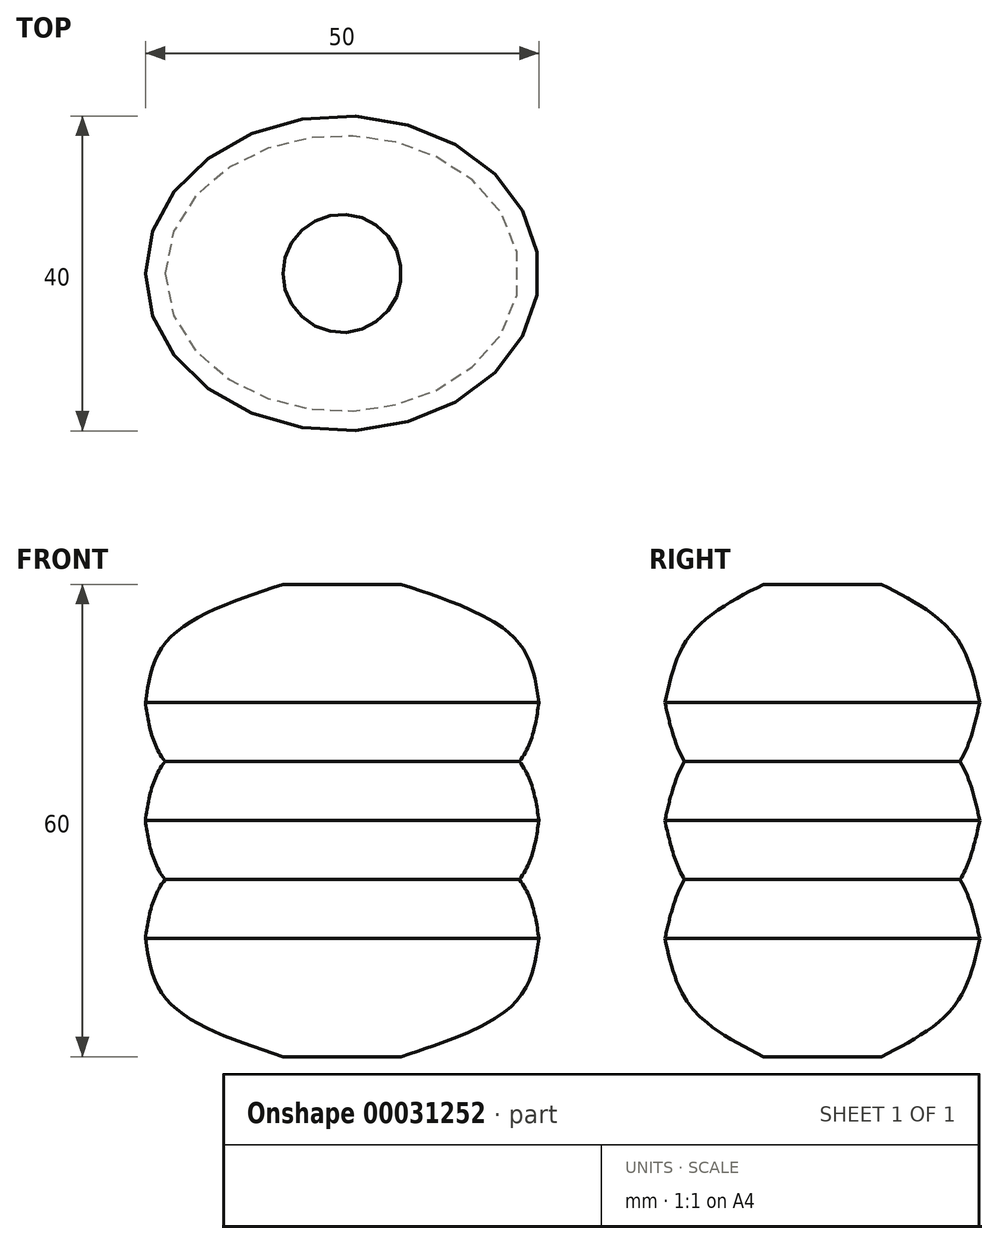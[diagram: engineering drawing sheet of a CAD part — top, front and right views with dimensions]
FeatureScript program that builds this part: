
annotation { "Feature Type Name" : "Feature", "Feature Type Description" : "" }
export const myFeature = defineFeature(function(context is Context, id is Id, definition is map)
    precondition{}
    {
        {
            var Q0;
            Q0=qCreatedBy(makeId("Top.planeOp"),FACE);
            var sketch = newSketch(context, id + "F0", { "sketchPlane" : qUnion([Q0])});
            skEllipse(sketch, "E0", {"center": v(0, 0) * mm, "majorRadius": 20 * mm, "minorRadius": 25 * mm, "majorAxis": v(0, 1)});
            skPoint(sketch, "E1", {"position": v(0, 20) * mm});
            skPoint(sketch, "E2", {"position": v(-25, 0) * mm});
            skSolve(sketch);
        }
        {
            var Q0;
            Q0=qCreatedBy(makeId("Top.planeOp"),FACE);
            cPlane(context, id + "F1", {"entities" : qUnion([Q0]), "cplaneType" : CPlaneType.OFFSET, "offset" : 15 * mm, "width" : 150 * mm, "height" : 150 * mm});
        }
        {
            var Q0;
            Q0=qCreatedBy(id+"F1.planeOp",FACE);
            var sketch = newSketch(context, id + "F2", { "sketchPlane" : qUnion([Q0])});
            skCircle(sketch, "E3", {"center": v(0, 0) * mm, "radius": 7.5 * mm});
            skSolve(sketch);
        }
        {
            var Q0;
            Q0=qCreatedBy(makeId("Top.planeOp"),FACE);
            cPlane(context, id + "F3", {"entities" : qUnion([Q0]), "cplaneType" : CPlaneType.OFFSET, "offset" : 7.5 * mm, "width" : 150 * mm, "height" : 150 * mm});
        }
        {
            var Q0;
            Q0=qCreatedBy(id+"F3.planeOp",FACE);
            var sketch = newSketch(context, id + "F4", { "sketchPlane" : qUnion([Q0])});
            skEllipse(sketch, "E4", {"center": v(0, 0) * mm, "majorRadius": 17.5 * mm, "minorRadius": 22.5 * mm, "majorAxis": v(0, -1)});
            skPoint(sketch, "E5", {"position": v(0, -17.5) * mm});
            skPoint(sketch, "E6", {"position": v(-22.5, 0) * mm});
            skSolve(sketch);
        }
        {
            var Q0;
            Q0=makeQuery(id+"F0.imprint","IMPRINT",FACE,{"disambiguationData":[TD([[makeQuery(id+"F0.imprint","IMPRINT",EDGE,{"derivedFrom":sQuery(id+"F0.wireOp",EDGE,"E0")}),1.0]])]});
            var Q1;
            Q1=makeQuery(id+"F4.imprint","IMPRINT",FACE,{"disambiguationData":[TD([[makeQuery(id+"F4.imprint","IMPRINT",EDGE,{"derivedFrom":sQuery(id+"F4.wireOp",EDGE,"E4")}),1.0]])]});
            var Q2;
            Q2=makeQuery(id+"F2.imprint","IMPRINT",FACE,{"disambiguationData":[TD([[makeQuery(id+"F2.imprint","IMPRINT",EDGE,{"derivedFrom":sQuery(id+"F2.wireOp",EDGE,"E3")}),1.0]])]});
            loft(context, id + "F5", {"sheetProfilesArray" : [{ "sheetProfileEntities" : qUnion([Q0]) }, { "sheetProfileEntities" : qUnion([Q1]) }, { "sheetProfileEntities" : qUnion([Q2]) }]});
        }
        {
            var Q0;
            Q0=makeQuery(id+"F5.opLoft","SWEPT_BODY",BODY,{"disambiguationData":[OSD([makeQuery(id+"F0.imprint","IMPRINT",FACE,{"disambiguationData":[TD([[makeQuery(id+"F0.imprint","IMPRINT",EDGE,{"derivedFrom":sQuery(id+"F0.wireOp",EDGE,"E0")}),1.0]])]}),makeQuery(id+"F2.imprint","IMPRINT",FACE,{"disambiguationData":[TD([[makeQuery(id+"F2.imprint","IMPRINT",EDGE,{"derivedFrom":sQuery(id+"F2.wireOp",EDGE,"E3")}),1.0]])]}),sQuery(id+"F4.wireOp",EDGE,"E4")])]});
            var Q1;
            Q1=qCreatedBy(makeId("Top.planeOp"),FACE);
            mirror(context, id + "F6", {"operationType" : NewBodyOperationType.ADD, "entities" : qUnion([Q0]), "mirrorPlane" : qUnion([Q1])});
        }
        {
            var Q0;
            Q0=makeQuery(id+"F5.opLoft","SWEPT_BODY",BODY,{"disambiguationData":[OSD([makeQuery(id+"F0.imprint","IMPRINT",FACE,{"disambiguationData":[TD([[makeQuery(id+"F0.imprint","IMPRINT",EDGE,{"derivedFrom":sQuery(id+"F0.wireOp",EDGE,"E0")}),1.0]])]}),makeQuery(id+"F2.imprint","IMPRINT",FACE,{"disambiguationData":[TD([[makeQuery(id+"F2.imprint","IMPRINT",EDGE,{"derivedFrom":sQuery(id+"F2.wireOp",EDGE,"E3")}),1.0]])]}),sQuery(id+"F4.wireOp",EDGE,"E4")])]});
            var Q1;
            Q1=qCreatedBy(id+"F3.planeOp",FACE);
            mirror(context, id + "F7", {"operationType" : NewBodyOperationType.ADD, "entities" : qUnion([Q0]), "mirrorPlane" : qUnion([Q1])});
        }
        {
            var Q0;
            Q0=makeQuery(id+"F5.opLoft","SWEPT_BODY",BODY,{"disambiguationData":[OSD([makeQuery(id+"F0.imprint","IMPRINT",FACE,{"disambiguationData":[TD([[makeQuery(id+"F0.imprint","IMPRINT",EDGE,{"derivedFrom":sQuery(id+"F0.wireOp",EDGE,"E0")}),1.0]])]}),makeQuery(id+"F2.imprint","IMPRINT",FACE,{"disambiguationData":[TD([[makeQuery(id+"F2.imprint","IMPRINT",EDGE,{"derivedFrom":sQuery(id+"F2.wireOp",EDGE,"E3")}),1.0]])]}),sQuery(id+"F4.wireOp",EDGE,"E4")])]});
            var Q1;
            Q1=qCreatedBy(makeId("Top.planeOp"),FACE);
            mirror(context, id + "F8", {"operationType" : NewBodyOperationType.ADD, "entities" : qUnion([Q0]), "mirrorPlane" : qUnion([Q1])});
        }
    });
